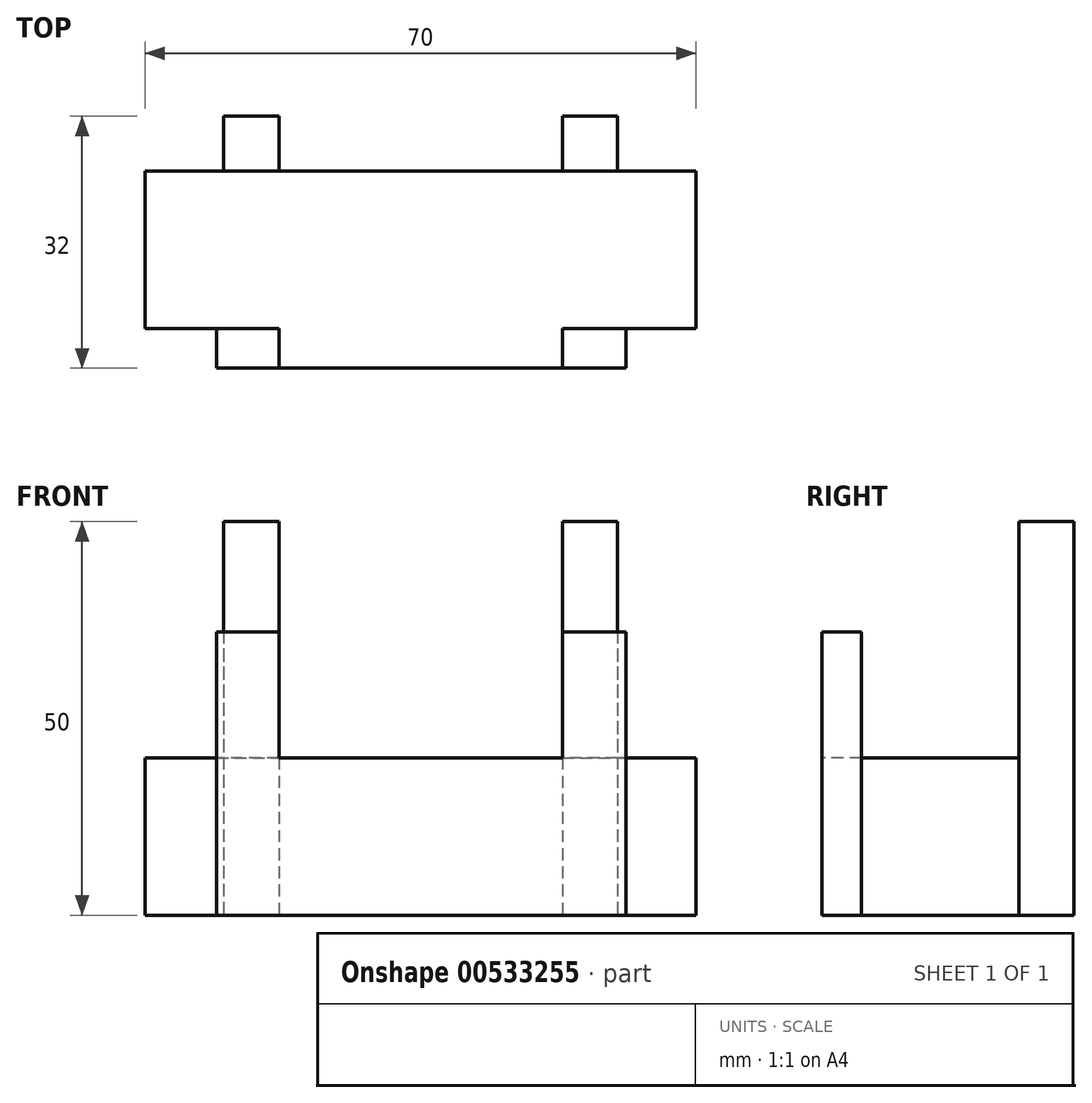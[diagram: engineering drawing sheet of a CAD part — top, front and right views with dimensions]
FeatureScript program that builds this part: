
annotation { "Feature Type Name" : "Feature", "Feature Type Description" : "" }
export const myFeature = defineFeature(function(context is Context, id is Id, definition is map)
    precondition{}
    {
        {
            var Q0;
            Q0=qCreatedBy(makeId("Top.planeOp"),FACE);
            var sketch = newSketch(context, id + "F0", { "sketchPlane" : qUnion([Q0])});
            skLineSegment(sketch, "E0.bottom", {"start": v(65.85, 22.37) * mm, "end": v(-4.15, 22.37) * mm});
            skLineSegment(sketch, "E0.top", {"start": v(65.85, 2.37) * mm, "end": v(-4.15, 2.37) * mm});
            skLineSegment(sketch, "E0.left", {"start": v(65.85, 22.37) * mm, "end": v(65.85, 2.37) * mm});
            skLineSegment(sketch, "E0.right", {"start": v(-4.15, 22.37) * mm, "end": v(-4.15, 2.37) * mm});
            skLineSegment(sketch, "E1.bottom", {"start": v(5.85, 22.37) * mm, "end": v(12.85, 22.37) * mm});
            skLineSegment(sketch, "E1.top", {"start": v(5.85, 29.37) * mm, "end": v(12.85, 29.37) * mm});
            skLineSegment(sketch, "E1.left", {"start": v(5.85, 22.37) * mm, "end": v(5.85, 29.37) * mm});
            skLineSegment(sketch, "E1.right", {"start": v(12.85, 22.37) * mm, "end": v(12.85, 29.37) * mm});
            skLineSegment(sketch, "E2.bottom", {"start": v(55.85, 22.37) * mm, "end": v(48.85, 22.37) * mm});
            skLineSegment(sketch, "E2.top", {"start": v(55.85, 29.37) * mm, "end": v(48.85, 29.37) * mm});
            skLineSegment(sketch, "E2.left", {"start": v(55.85, 22.37) * mm, "end": v(55.85, 29.37) * mm});
            skLineSegment(sketch, "E2.right", {"start": v(48.85, 22.37) * mm, "end": v(48.85, 29.37) * mm});
            skSolve(sketch);
        }
        {
            var Q0;
            Q0=qSketchRegion(id+"F0",true);
            extrude(context, id + "F1", {"entities" : qUnion([Q0]), "depth" : 10 * mm});
        }
        {
            var Q0;
            Q0=makeQuery(id+"F1.opExtrude","CAP_FACE",FACE,{"disambiguationData":[OSD([sQuery(id+"F0.wireOp",EDGE,"E0.bottom"),sQuery(id+"F0.wireOp",EDGE,"E0.top"),sQuery(id+"F0.wireOp",EDGE,"E0.left"),sQuery(id+"F0.wireOp",EDGE,"E0.right"),sQuery(id+"F0.wireOp",EDGE,"E1.top"),sQuery(id+"F0.wireOp",EDGE,"E1.left"),sQuery(id+"F0.wireOp",EDGE,"E1.right"),sQuery(id+"F0.wireOp",EDGE,"E2.top"),sQuery(id+"F0.wireOp",EDGE,"E2.left"),sQuery(id+"F0.wireOp",EDGE,"E2.right")])],"isStart":false});
            var sketch = newSketch(context, id + "F2", { "sketchPlane" : qUnion([Q0])});
            skLineSegment(sketch, "E3", {"start": v(55.85, 22.37) * mm, "end": v(48.85, 22.37) * mm});
            skLineSegment(sketch, "E4", {"start": v(48.85, 22.37) * mm, "end": v(12.85, 22.37) * mm});
            skLineSegment(sketch, "E5", {"start": v(12.85, 22.37) * mm, "end": v(5.85, 22.37) * mm});
            skSolve(sketch);
        }
        {
            var Q0;
            Q0=makeQuery(id+"F2.imprint","IMPRINT",FACE,{"disambiguationData":[TD([[makeQuery(id+"F2.imprint","IMPRINT",EDGE,{"derivedFrom":sQuery(id+"F2.wireOp",EDGE,"E5")}),-1.0]])]});
            var Q1;
            Q1=makeQuery(id+"F2.imprint","IMPRINT",FACE,{"disambiguationData":[TD([[makeQuery(id+"F2.imprint","IMPRINT",EDGE,{"derivedFrom":sQuery(id+"F2.wireOp",EDGE,"E3")}),-1.0]])]});
            extrude(context, id + "F3", {"entities" : qUnion([Q0, Q1]), "operationType" : NewBodyOperationType.ADD, "depth" : 30 * mm});
        }
        {
            var Q0;
            Q0=makeQuery(id+"F1.opExtrude","SWEPT_FACE",FACE,{"disambiguationData":[OSD([sQuery(id+"F0.wireOp",EDGE,"E0.top")])]});
            var sketch = newSketch(context, id + "F4", { "sketchPlane" : qUnion([Q0])});
            skLineSegment(sketch, "E6.bottom", {"start": v(4.94, 0) * mm, "end": v(56.96, 0) * mm});
            skLineSegment(sketch, "E6.top", {"start": v(4.94, 10) * mm, "end": v(56.96, 10) * mm});
            skLineSegment(sketch, "E6.left", {"start": v(4.94, 0) * mm, "end": v(4.94, 10) * mm});
            skLineSegment(sketch, "E6.right", {"start": v(56.96, 0) * mm, "end": v(56.96, 10) * mm});
            skSolve(sketch);
        }
        {
            var Q0;
            Q0=makeQuery(id+"F4.imprint","IMPRINT",FACE,{"disambiguationData":[TD([[makeQuery(id+"F4.imprint","IMPRINT",EDGE,{"derivedFrom":sQuery(id+"F4.wireOp",EDGE,"E6.bottom")}),-1.0]])]});
            extrude(context, id + "F5", {"entities" : qUnion([Q0]), "operationType" : NewBodyOperationType.ADD, "depth" : 5 * mm});
        }
        {
            var Q0;
            Q0=makeQuery(id+"F5.boolean.opBoolean","MERGE",FACE,{"derivedFrom":[makeQuery(id+"F1.opExtrude","CAP_FACE",FACE,{"disambiguationData":[OSD([sQuery(id+"F0.wireOp",EDGE,"E0.bottom"),sQuery(id+"F0.wireOp",EDGE,"E0.top"),sQuery(id+"F0.wireOp",EDGE,"E0.left"),sQuery(id+"F0.wireOp",EDGE,"E0.right"),sQuery(id+"F0.wireOp",EDGE,"E1.top"),sQuery(id+"F0.wireOp",EDGE,"E1.left"),sQuery(id+"F0.wireOp",EDGE,"E1.right"),sQuery(id+"F0.wireOp",EDGE,"E2.top"),sQuery(id+"F0.wireOp",EDGE,"E2.left"),sQuery(id+"F0.wireOp",EDGE,"E2.right")])],"isStart":false}),makeQuery(id+"F5.opExtrude","SWEPT_FACE",FACE,{"disambiguationData":[OSD([sQuery(id+"F4.wireOp",EDGE,"E6.top")])]})]});
            var sketch = newSketch(context, id + "F6", { "sketchPlane" : qUnion([Q0])});
            skLineSegment(sketch, "E7", {"start": v(4.94, 2.37) * mm, "end": v(56.96, 2.37) * mm});
            skSolve(sketch);
        }
        {
            var Q0;
            Q0=makeQuery(id+"F6.imprint","IMPRINT",FACE,{"disambiguationData":[TD([[makeQuery(id+"F6.imprint","IMPRINT",EDGE,{"derivedFrom":sQuery(id+"F6.wireOp",EDGE,"E7")}),-1.0]])]});
            extrude(context, id + "F7", {"entities" : qUnion([Q0]), "operationType" : NewBodyOperationType.ADD, "depth" : 16 * mm});
        }
        {
            var Q0;
            {var subQ0=sQuery(id+"F4.wireOp",EDGE,"E6.top");Q0=makeQuery(id+"F7.boolean.opBoolean","MERGE",FACE,{"derivedFrom":[makeQuery(id+"F5.opExtrude","CAP_FACE",FACE,{"disambiguationData":[OSD([sQuery(id+"F4.wireOp",EDGE,"E6.bottom"),subQ0,sQuery(id+"F4.wireOp",EDGE,"E6.left"),sQuery(id+"F4.wireOp",EDGE,"E6.right")])],"isStart":false}),makeQuery(id+"F7.opExtrude","SWEPT_FACE",FACE,{"disambiguationData":[OSD([subQ0])]})]});}
            var sketch = newSketch(context, id + "F8", { "sketchPlane" : qUnion([Q0])});
            skLineSegment(sketch, "E8.bottom", {"start": v(12.85, 26) * mm, "end": v(48.85, 26) * mm});
            skLineSegment(sketch, "E8.top", {"start": v(12.85, 10) * mm, "end": v(48.85, 10) * mm});
            skLineSegment(sketch, "E8.left", {"start": v(12.85, 26) * mm, "end": v(12.85, 10) * mm});
            skLineSegment(sketch, "E8.right", {"start": v(48.85, 26) * mm, "end": v(48.85, 10) * mm});
            skSolve(sketch);
        }
        {
            var Q0;
            Q0=makeQuery(id+"F8.imprint","IMPRINT",FACE,{"disambiguationData":[TD([[makeQuery(id+"F8.imprint","IMPRINT",EDGE,{"derivedFrom":sQuery(id+"F8.wireOp",EDGE,"E8.bottom")}),1.0]])]});
            extrude(context, id + "F9", {"entities" : qUnion([Q0]), "operationType" : NewBodyOperationType.REMOVE, "oppositeDirection" : true, "depth" : 25 * mm});
        }
        {
            var Q0;
            Q0=makeQuery(id+"F8.imprint","IMPRINT",FACE,{"disambiguationData":[TD([[makeQuery(id+"F8.imprint","IMPRINT",EDGE,{"derivedFrom":sQuery(id+"F8.wireOp",EDGE,"E8.bottom")}),1.0]])]});
            extrude(context, id + "F10", {"entities" : qUnion([Q0]), "operationType" : NewBodyOperationType.REMOVE, "oppositeDirection" : true, "depth" : 25 * mm, "offsetDistance" : 25 * mm});
        }
        {
            var Q0;
            Q0=makeQuery(id+"F5.boolean.opBoolean","MERGE",FACE,{"derivedFrom":[makeQuery(id+"F1.opExtrude","CAP_FACE",FACE,{"disambiguationData":[OSD([sQuery(id+"F0.wireOp",EDGE,"E0.bottom"),sQuery(id+"F0.wireOp",EDGE,"E0.top"),sQuery(id+"F0.wireOp",EDGE,"E0.left"),sQuery(id+"F0.wireOp",EDGE,"E0.right"),sQuery(id+"F0.wireOp",EDGE,"E1.top"),sQuery(id+"F0.wireOp",EDGE,"E1.left"),sQuery(id+"F0.wireOp",EDGE,"E1.right"),sQuery(id+"F0.wireOp",EDGE,"E2.top"),sQuery(id+"F0.wireOp",EDGE,"E2.left"),sQuery(id+"F0.wireOp",EDGE,"E2.right")])],"isStart":true}),makeQuery(id+"F5.opExtrude","SWEPT_FACE",FACE,{"disambiguationData":[OSD([sQuery(id+"F4.wireOp",EDGE,"E6.bottom")])]})]});
            extrude(context, id + "F11", {"entities" : qUnion([Q0]), "operationType" : NewBodyOperationType.ADD, "depth" : 10 * mm, "offsetDistance" : 25 * mm});
        }
    });
